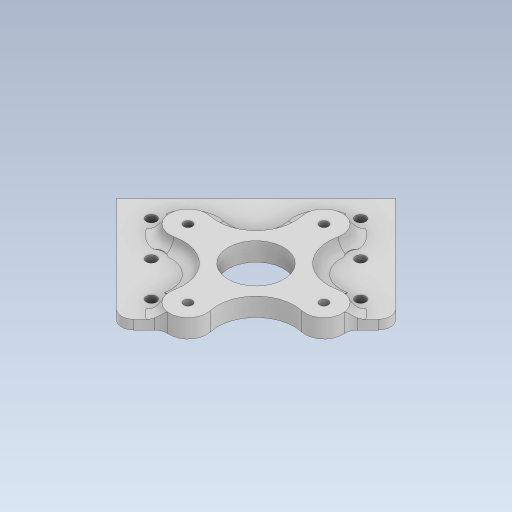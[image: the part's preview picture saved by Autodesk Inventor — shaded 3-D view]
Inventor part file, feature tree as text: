
AUTODESK INVENTOR PART (.ipt)
format: ipt  version: 2023 (Build 270158000, 158)  size: 296,448 bytes
history: native  units: in
note: dims shown in document units (in); Inventor stores cm internally (conversion verified against a paired STEP export)
features: sketch x3, extrude x3, projected_geometry x2, hole x1, fillet x1
ambient origin geometry x8: Origin, YZ Plane, XZ Plane, XY Plane, X Axis, Y Axis, Z Axis, Center Point
bodies: Solid1 (feature_tree)
feature tree (10):
  sketch  "Sketch1"  dims[d0=0.75in d1=1.5748in d3=360.0deg]
  extrude  "Extrusion1"  Depth=1.5748in TaperAngle=360.0deg
  hole  "Hole1"  [1 undecoded]
  extrude  "Extrusion2"  Depth=0.25in TaperAngle=360.0deg
  fillet  "Fillet1"  Radius=0.375in
  extrude  "Extrusion3"  Depth=0.25in
  sketch  "Sketch2"  dims[d5=1.378in d6=1.125in]
  projected_geometry  "Projected Loop1"
  sketch  "Sketch3"  dims[d7=1.625in d8=1.5748in d10=360.0deg d12=0.375in d13=0.0in d14=0.1772in d15=0.75in d16=0.2067in d17=0.1969in d18=0.5635in d19=1.0in d20=0.8108in d21=0.5in d22=4.0in d23=3.0in d24=0.5in d25=45.0deg d26=1.1811in d28=1.0in d29=0.7874in d31=3.0in d34=3.0in d35=1.125in d36=0.2087in d37=0.1875in d38=0.0in d39=0.25in d40=0.5in d41=0.5in d42=0.5in d43=0.5in d44=0.5in d45=0.5in d46=0.1875in d47=0.0in]
  projected_geometry  "Projected Loop2"
note: 1 required parameter value undecoded (feature->parameter linkage not recoverable at this tier; creation-order binding heuristic only, values carry confidence <= 0.55)
